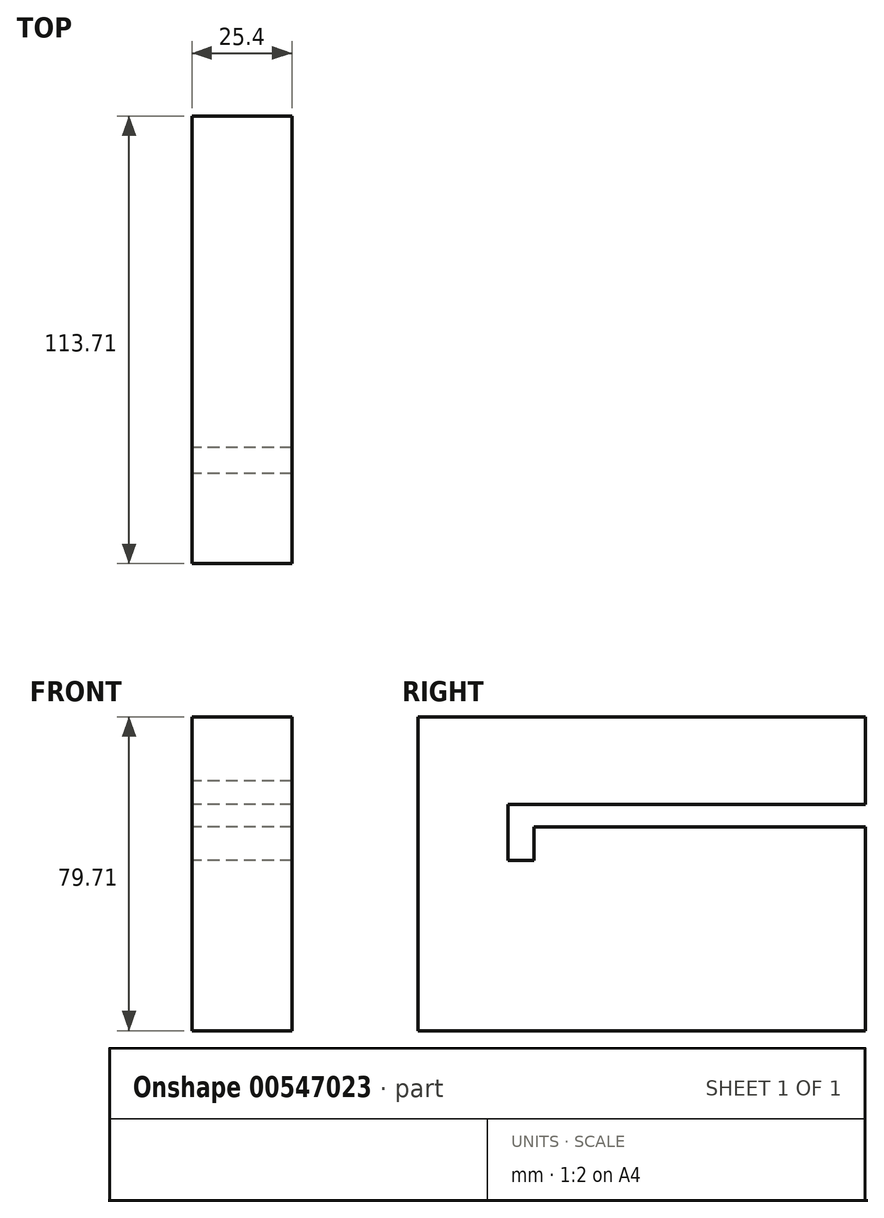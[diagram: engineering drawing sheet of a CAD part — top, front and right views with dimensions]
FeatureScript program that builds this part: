
annotation { "Feature Type Name" : "Feature", "Feature Type Description" : "" }
export const myFeature = defineFeature(function(context is Context, id is Id, definition is map)
    precondition{}
    {
        {
            var Q0;
            Q0=qCreatedBy(makeId("Right.planeOp"),FACE);
            var sketch = newSketch(context, id + "F0", { "sketchPlane" : qUnion([Q0])});
            skLineSegment(sketch, "E0.bottom", {"start": v(-56.85, 21.66) * mm, "end": v(56.85, 21.66) * mm});
            skLineSegment(sketch, "E0.top", {"start": v(-56.85, -21.66) * mm, "end": v(56.85, -21.66) * mm});
            skLineSegment(sketch, "E0.left", {"start": v(-56.85, 21.66) * mm, "end": v(-56.85, -21.66) * mm});
            skLineSegment(sketch, "E0.right", {"start": v(56.85, 21.66) * mm, "end": v(56.85, -21.66) * mm});
            skPoint(sketch, "E0.middle", {"position": v(0, 0) * mm});
            skLineSegment(sketch, "E1.bottom", {"start": v(-56.85, 21.66) * mm, "end": v(-33.99, 21.66) * mm});
            skLineSegment(sketch, "E1.top", {"start": v(-56.85, 41.8) * mm, "end": v(-33.99, 41.8) * mm});
            skLineSegment(sketch, "E1.left", {"start": v(-56.85, 21.66) * mm, "end": v(-56.85, 41.8) * mm});
            skLineSegment(sketch, "E1.right", {"start": v(-33.99, 21.66) * mm, "end": v(-33.99, 41.8) * mm});
            skLineSegment(sketch, "E2.bottom", {"start": v(56.85, 21.66) * mm, "end": v(-27.37, 21.66) * mm});
            skLineSegment(sketch, "E2.top", {"start": v(56.85, 30.08) * mm, "end": v(-27.37, 30.08) * mm});
            skLineSegment(sketch, "E2.left", {"start": v(56.85, 21.66) * mm, "end": v(56.85, 30.08) * mm});
            skLineSegment(sketch, "E2.right", {"start": v(-27.37, 21.66) * mm, "end": v(-27.37, 30.08) * mm});
            skLineSegment(sketch, "E3.bottom", {"start": v(-33.99, 41.8) * mm, "end": v(56.85, 41.8) * mm});
            skLineSegment(sketch, "E3.top", {"start": v(-33.99, 35.8) * mm, "end": v(56.85, 35.8) * mm});
            skLineSegment(sketch, "E3.left", {"start": v(-33.99, 41.8) * mm, "end": v(-33.99, 35.8) * mm});
            skLineSegment(sketch, "E3.right", {"start": v(56.85, 41.8) * mm, "end": v(56.85, 35.8) * mm});
            skLineSegment(sketch, "E4.bottom", {"start": v(-33.99, 41.8) * mm, "end": v(56.86, 41.8) * mm});
            skLineSegment(sketch, "E4.top", {"start": v(-33.99, 58.05) * mm, "end": v(56.86, 58.05) * mm});
            skLineSegment(sketch, "E4.left", {"start": v(-33.99, 41.8) * mm, "end": v(-33.99, 58.05) * mm});
            skLineSegment(sketch, "E4.right", {"start": v(56.86, 41.8) * mm, "end": v(56.86, 58.05) * mm});
            skLineSegment(sketch, "E5.bottom", {"start": v(-33.99, 58.05) * mm, "end": v(-56.85, 58.05) * mm});
            skLineSegment(sketch, "E5.top", {"start": v(-33.99, 41.8) * mm, "end": v(-56.85, 41.8) * mm});
            skLineSegment(sketch, "E5.left", {"start": v(-33.99, 58.05) * mm, "end": v(-33.99, 41.8) * mm});
            skLineSegment(sketch, "E5.right", {"start": v(-56.85, 58.05) * mm, "end": v(-56.85, 41.8) * mm});
            skLineSegment(sketch, "E6.0", {"start": v(-33.99, -11.53) * mm, "end": v(56.86, -11.53) * mm});
            skSolve(sketch);
        }
        {
            var Q0;
            Q0 = qSketchRegion(id + "F0", true);
            extrude(context, id + "F1", {"entities" : qUnion([Q0]), "depth" : 25.4 * mm, "offsetDistance" : 25.4 * mm});
        }
    });
